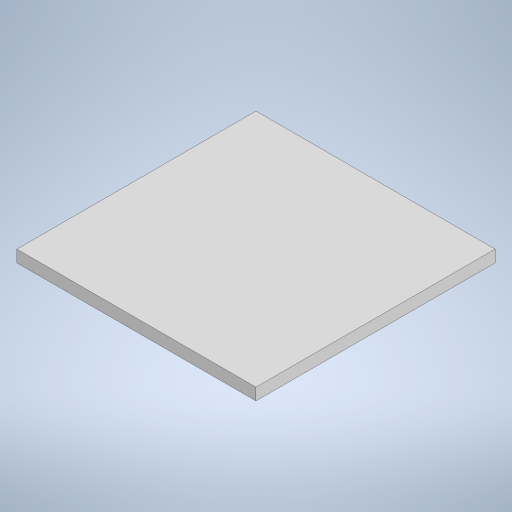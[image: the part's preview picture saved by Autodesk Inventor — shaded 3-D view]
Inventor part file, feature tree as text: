
AUTODESK INVENTOR PART (.ipt)
format: ipt  version: 2024 (Build 280153000, 153)  size: 198,144 bytes
history: native  units: mm
features: extrude x1, sketch x1
ambient origin geometry x8: Origin, YZ Plane, XZ Plane, XY Plane, X Axis, Y Axis, Z Axis, Center Point
bodies: Solid1 (feature_tree)
feature tree (2):
  extrude  "Extrusion1"  Depth=200.0mm
  sketch  "Sketch1"  dims[d0=200.0mm d1=200.0mm d2=10.0mm d3=0.0mm]
